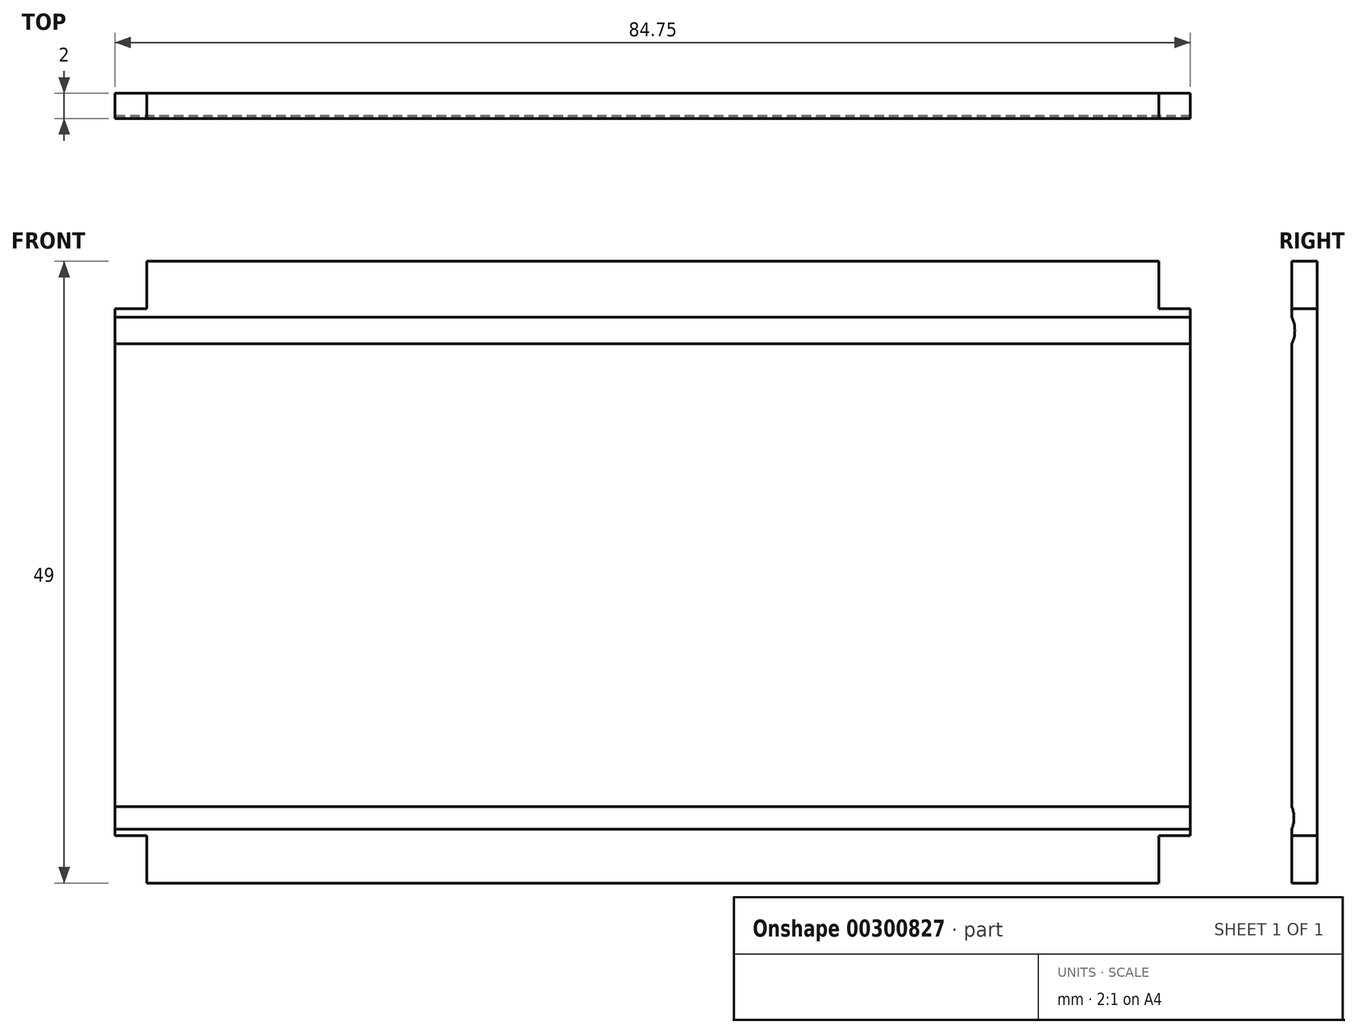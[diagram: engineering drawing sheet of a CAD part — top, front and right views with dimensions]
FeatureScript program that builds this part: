
annotation { "Feature Type Name" : "Feature", "Feature Type Description" : "" }
export const myFeature = defineFeature(function(context is Context, id is Id, definition is map)
    precondition{}
    {
        {
            var Q0;
            Q0=qCreatedBy(makeId("Front.planeOp"),FACE);
            var sketch = newSketch(context, id + "F0", { "sketchPlane" : qUnion([Q0])});
            skLineSegment(sketch, "E0.bottom", {"start": v(0, 0) * mm, "end": v(1695, 0) * mm});
            skLineSegment(sketch, "E0.top", {"start": v(0, -980) * mm, "end": v(1695, -980) * mm});
            skLineSegment(sketch, "E0.left", {"start": v(0, 0) * mm, "end": v(0, -980) * mm});
            skLineSegment(sketch, "E0.right", {"start": v(1695, 0) * mm, "end": v(1695, -980) * mm});
            skPoint(sketch, "E1.visualSharp", {"position": v(1551.45, -62.15) * mm});
            skSolve(sketch);
        }
        {
            var Q0;
            Q0=makeQuery(id+"F0.imprint","IMPRINT",FACE,{"disambiguationData":[TD([[makeQuery(id+"F0.imprint","IMPRINT",EDGE,{"derivedFrom":sQuery(id+"F0.wireOp",EDGE,"E0.bottom")}),-1.0]])]});
            extrude(context, id + "F1", {"entities" : qUnion([Q0]), "depth" : 40 * mm});
        }
        {
            var Q0;
            Q0=makeQuery(id+"F1.opExtrude","SWEPT_FACE",FACE,{"disambiguationData":[OSD([sQuery(id+"F0.wireOp",EDGE,"E0.left")])]});
            var sketch = newSketch(context, id + "F2", { "sketchPlane" : qUnion([Q0])});
            skCircle(sketch, "E2", {"center": v(85.36, -109.13) * mm, "radius": 50 * mm});
            skCircle(sketch, "E3", {"center": v(86.77, -877.35) * mm, "radius": 50 * mm});
            skSolve(sketch);
        }
        {
            var Q0;
            Q0=qSketchRegion(id+"F2",true);
            extrude(context, id + "F3", {"entities" : qUnion([Q0]), "operationType" : NewBodyOperationType.REMOVE, "endBound" : BoundingType.THROUGH_ALL, "oppositeDirection" : true, "depth" : 25 * mm});
        }
        {
            var Q0;
            Q0=makeQuery(id+"F1.opExtrude","SWEPT_FACE",FACE,{"disambiguationData":[OSD([sQuery(id+"F0.wireOp",EDGE,"E0.bottom")])]});
            var sketch = newSketch(context, id + "F4", { "sketchPlane" : qUnion([Q0])});
            skCircle(sketch, "E4", {"center": v(140.8, -82.49) * mm, "radius": 50 * mm});
            skCircle(sketch, "E5", {"center": v(1551.46, -85.07) * mm, "radius": 50 * mm});
            skSolve(sketch);
        }
        {
            var Q0;
            {var subQ0=sQuery(id+"F4.wireOp",EDGE,"E4");var subQ1=makeQuery(id+"F1.opExtrude","CAP_EDGE",EDGE,{"disambiguationData":[OSD([sQuery(id+"F0.wireOp",EDGE,"E0.bottom")])],"isStart":false});var subQ2=makeQuery(id+"F4.imprint","INTERSECT",VERTEX,{"disambiguationData":[OD(0.0)],"derivedFrom":[subQ1,subQ0]});Q0=makeQuery(id+"F4.imprint","IMPRINT",FACE,{"disambiguationData":[TD([[makeQuery(id+"F4.imprint","IMPRINT",EDGE,{"disambiguationData":[TD([[subQ2,-1.0]])],"derivedFrom":subQ0}),1.0]])]});}
            var Q1;
            {var subQ0=sQuery(id+"F4.wireOp",EDGE,"E5");var subQ1=makeQuery(id+"F1.opExtrude","CAP_EDGE",EDGE,{"disambiguationData":[OSD([sQuery(id+"F0.wireOp",EDGE,"E0.bottom")])],"isStart":false});var subQ2=makeQuery(id+"F4.imprint","INTERSECT",VERTEX,{"disambiguationData":[OD(0.0)],"derivedFrom":[subQ1,subQ0]});Q1=makeQuery(id+"F4.imprint","IMPRINT",FACE,{"disambiguationData":[TD([[makeQuery(id+"F4.imprint","IMPRINT",EDGE,{"disambiguationData":[TD([[subQ2,1.0]])],"derivedFrom":subQ0}),1.0]])]});}
            extrude(context, id + "F5", {"entities" : qUnion([Q0, Q1]), "operationType" : NewBodyOperationType.REMOVE, "endBound" : BoundingType.THROUGH_ALL, "oppositeDirection" : true, "depth" : 850 * mm});
        }
        {
            var Q0;
            Q0=makeQuery(id+"F1.opExtrude","SWEPT_FACE",FACE,{"disambiguationData":[OSD([sQuery(id+"F0.wireOp",EDGE,"E0.left")])]});
            var sketch = newSketch(context, id + "F6", { "sketchPlane" : qUnion([Q0])});
            skLineSegment(sketch, "E6", {"start": v(0, 0) * mm, "end": v(40, 0) * mm});
            skLineSegment(sketch, "E7", {"start": v(40, 0) * mm, "end": v(40, -75) * mm});
            skLineSegment(sketch, "E8", {"start": v(40, -75) * mm, "end": v(0, -75) * mm});
            skLineSegment(sketch, "E9", {"start": v(0, -75) * mm, "end": v(0, 0) * mm});
            skLineSegment(sketch, "E10", {"start": v(40, -980) * mm, "end": v(0, -980) * mm});
            skLineSegment(sketch, "E11", {"start": v(0, -980) * mm, "end": v(0, -905) * mm});
            skLineSegment(sketch, "E12", {"start": v(0, -905) * mm, "end": v(40, -905) * mm});
            skLineSegment(sketch, "E13", {"start": v(40, -905) * mm, "end": v(40, -980) * mm});
            skSolve(sketch);
        }
        {
            var Q0;
            Q0=makeQuery(id+"F6.imprint","IMPRINT",FACE,{"disambiguationData":[TD([[makeQuery(id+"F6.imprint","IMPRINT",EDGE,{"derivedFrom":sQuery(id+"F6.wireOp",EDGE,"E6")}),1.0]])]});
            var Q1;
            Q1=makeQuery(id+"F6.imprint","IMPRINT",FACE,{"disambiguationData":[TD([[makeQuery(id+"F6.imprint","IMPRINT",EDGE,{"derivedFrom":sQuery(id+"F6.wireOp",EDGE,"E10")}),-1.0]])]});
            extrude(context, id + "F7", {"entities" : qUnion([Q0, Q1]), "operationType" : NewBodyOperationType.REMOVE, "oppositeDirection" : true, "depth" : 50 * mm});
        }
        {
            var Q0;
            Q0=makeQuery(id+"F1.opExtrude","SWEPT_FACE",FACE,{"disambiguationData":[OSD([sQuery(id+"F0.wireOp",EDGE,"E0.right")])]});
            var sketch = newSketch(context, id + "F8", { "sketchPlane" : qUnion([Q0])});
            skLineSegment(sketch, "E14", {"start": v(-40, 0) * mm, "end": v(0, 0) * mm});
            skLineSegment(sketch, "E15", {"start": v(0, 0) * mm, "end": v(0, -75) * mm});
            skLineSegment(sketch, "E16", {"start": v(0, -75) * mm, "end": v(-40, -75) * mm});
            skLineSegment(sketch, "E17", {"start": v(-40, -75) * mm, "end": v(-40, 0) * mm});
            skLineSegment(sketch, "E18", {"start": v(0, -980) * mm, "end": v(-40, -980) * mm});
            skLineSegment(sketch, "E19", {"start": v(-40, -980) * mm, "end": v(-40, -905) * mm});
            skLineSegment(sketch, "E20", {"start": v(-40, -905) * mm, "end": v(0, -905) * mm});
            skLineSegment(sketch, "E21", {"start": v(0, -905) * mm, "end": v(0, -980) * mm});
            skSolve(sketch);
        }
        {
            var Q0;
            Q0=makeQuery(id+"F8.imprint","IMPRINT",FACE,{"disambiguationData":[TD([[makeQuery(id+"F8.imprint","IMPRINT",EDGE,{"derivedFrom":sQuery(id+"F8.wireOp",EDGE,"E14")}),-1.0]])]});
            var Q1;
            Q1=makeQuery(id+"F8.imprint","IMPRINT",FACE,{"disambiguationData":[TD([[makeQuery(id+"F8.imprint","IMPRINT",EDGE,{"derivedFrom":sQuery(id+"F8.wireOp",EDGE,"E18")}),1.0]])]});
            extrude(context, id + "F9", {"entities" : qUnion([Q0, Q1]), "operationType" : NewBodyOperationType.REMOVE, "oppositeDirection" : true, "depth" : 50 * mm});
        }
        {
            var Q0;
            Q0=makeQuery(id+"F1.opExtrude","SWEPT_BODY",BODY,{"disambiguationData":[OSD([sQuery(id+"F0.wireOp",EDGE,"E0.bottom"),sQuery(id+"F0.wireOp",EDGE,"E0.top"),sQuery(id+"F0.wireOp",EDGE,"E0.left"),sQuery(id+"F0.wireOp",EDGE,"E0.right")])]});
            var Q1;
            Q1=qCreatedBy(makeId("Origin.pointOp"),VERTEX);
            transform(context, id + "F10", {"entities" : qUnion([Q0]), "transformType" : TransformType.SCALE_UNIFORMLY, "scale" : 0.05, "scalePoint" : qUnion([Q1]), "makeCopy" : false});
        }
    });
